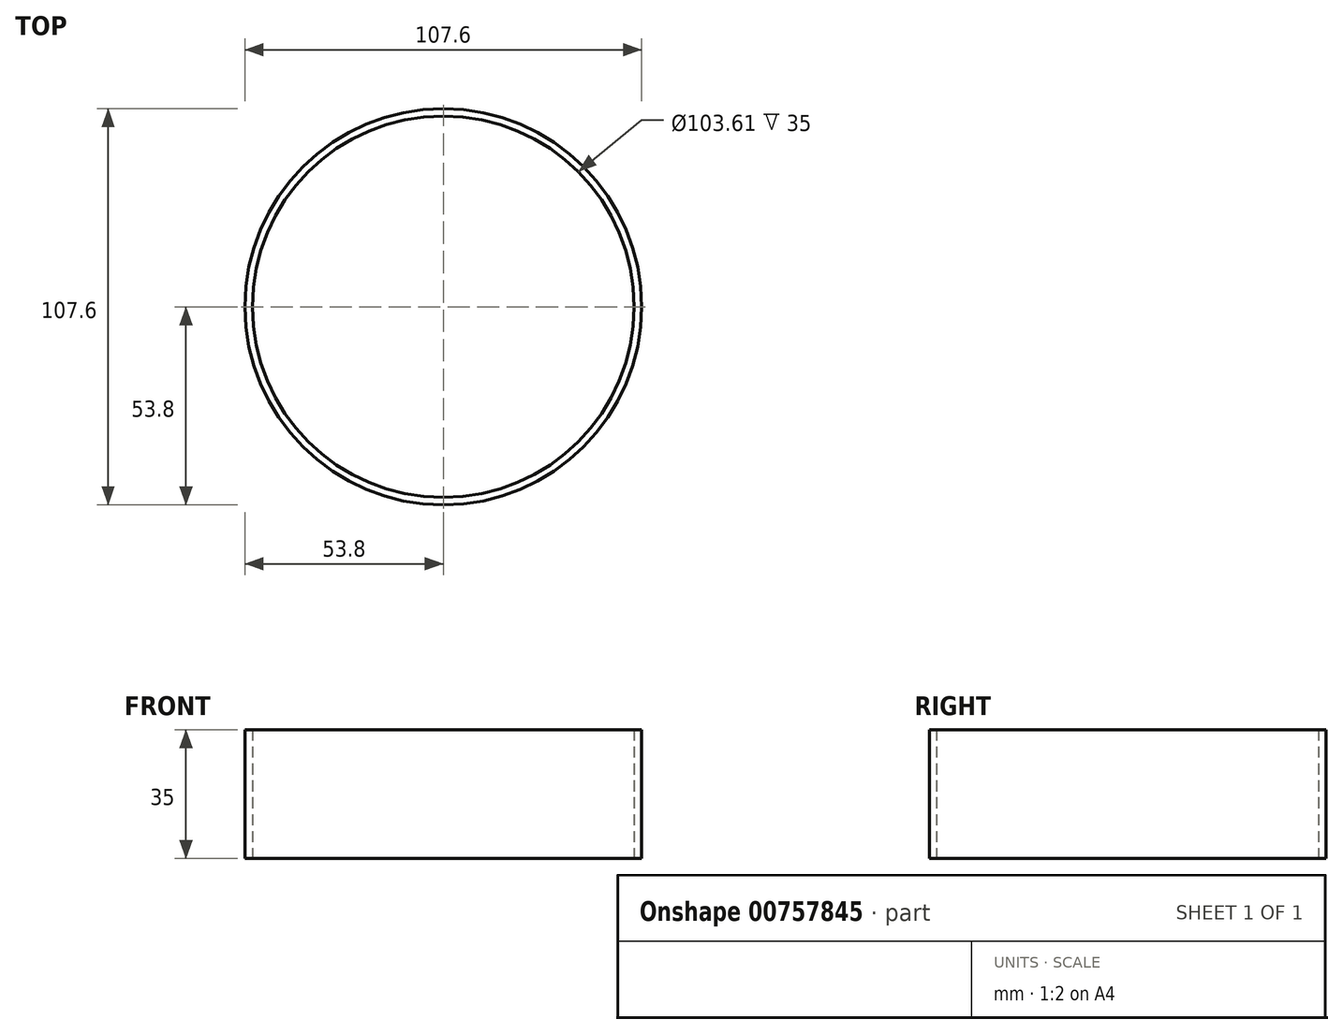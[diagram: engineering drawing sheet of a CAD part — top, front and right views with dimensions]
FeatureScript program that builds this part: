
annotation { "Feature Type Name" : "Feature", "Feature Type Description" : "" }
export const myFeature = defineFeature(function(context is Context, id is Id, definition is map)
    precondition{}
    {
        {
            var Q0;
            Q0=qCreatedBy(makeId("Top.planeOp"),FACE);
            var sketch = newSketch(context, id + "F0", { "sketchPlane" : qUnion([Q0])});
            skCircle(sketch, "E0", {"center": v(0, 0) * mm, "radius": 51.8 * mm});
            skCircle(sketch, "E1", {"center": v(0, 0) * mm, "radius": 53.8 * mm});
            skSolve(sketch);
        }
        {
            var Q0;
            Q0=makeQuery(id+"F0.imprint","IMPRINT",FACE,{"disambiguationData":[TD([[makeQuery(id+"F0.imprint","IMPRINT",EDGE,{"derivedFrom":sQuery(id+"F0.wireOp",EDGE,"E0")}),-1.0]])]});
            extrude(context, id + "F1", {"entities" : qUnion([Q0]), "depth" : 35 * mm, "offsetDistance" : 25.4 * mm});
        }
    });
